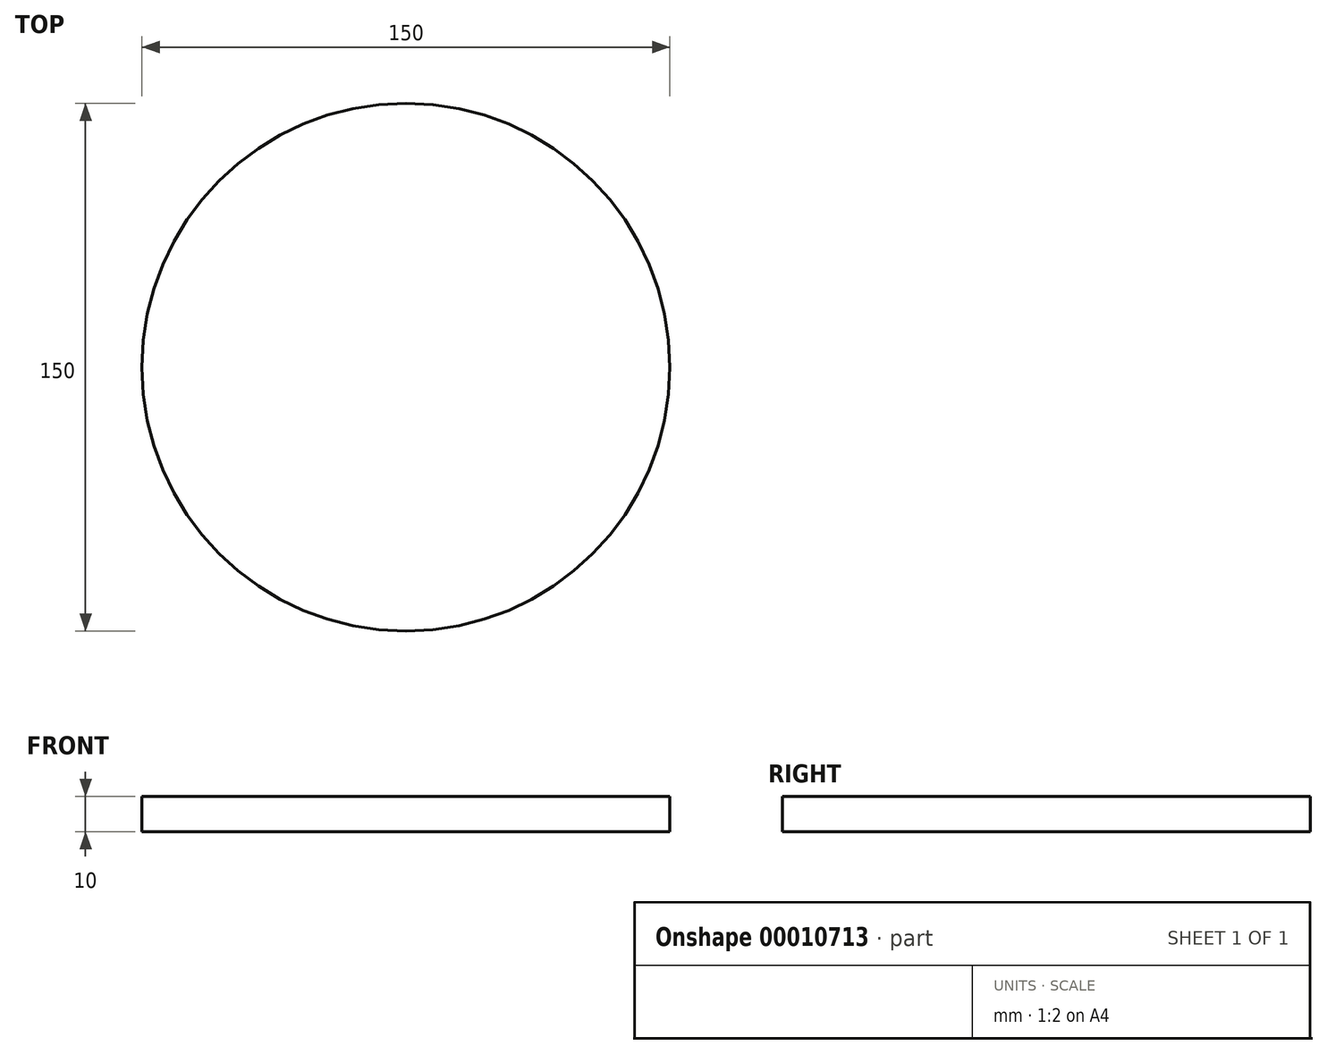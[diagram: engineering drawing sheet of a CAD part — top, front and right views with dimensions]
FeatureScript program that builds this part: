
annotation { "Feature Type Name" : "Feature", "Feature Type Description" : "" }
export const myFeature = defineFeature(function(context is Context, id is Id, definition is map)
    precondition{}
    {
        {
            var Q0;
            Q0=qCreatedBy(makeId("Top.planeOp"),FACE);
            var sketch = newSketch(context, id + "F0", { "sketchPlane" : qUnion([Q0])});
            skCircle(sketch, "E0", {"center": v(0, 0) * mm, "radius": 75 * mm});
            skCircle(sketch, "E1", {"center": v(0, 0) * mm, "radius": 75.55 * mm});
            skSolve(sketch);
        }
        {
            var Q0;
            Q0=makeQuery(id+"F0.imprint","IMPRINT",FACE,{"disambiguationData":[TD([[makeQuery(id+"F0.imprint","IMPRINT",EDGE,{"derivedFrom":sQuery(id+"F0.wireOp",EDGE,"E0")}),1.0]])]});
            extrude(context, id + "F1", {"entities" : qUnion([Q0]), "depth" : 10 * mm});
        }
    });
